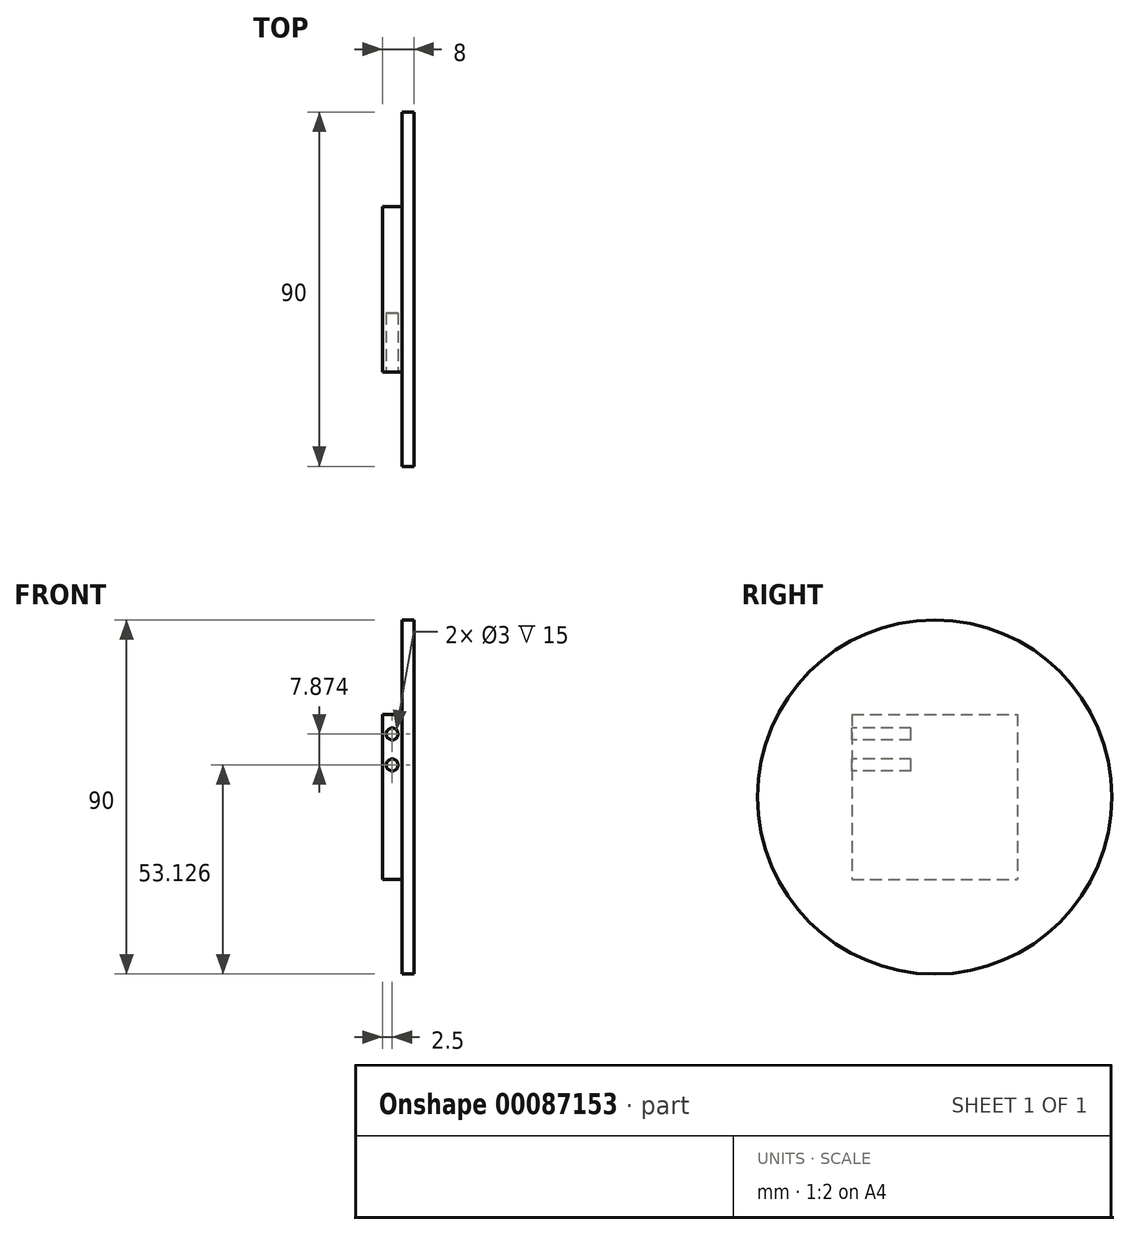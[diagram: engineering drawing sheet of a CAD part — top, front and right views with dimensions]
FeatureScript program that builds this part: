
annotation { "Feature Type Name" : "Feature", "Feature Type Description" : "" }
export const myFeature = defineFeature(function(context is Context, id is Id, definition is map)
    precondition{}
    {
        {
            var Q0;
            Q0=qCreatedBy(makeId("Right.planeOp"),FACE);
            var sketch = newSketch(context, id + "F0", { "sketchPlane" : qUnion([Q0])});
            skCircle(sketch, "E0", {"center": v(0, 0) * mm, "radius": 45 * mm, "construction": true});
            skLineSegment(sketch, "E1.bottom", {"start": v(-21, 21) * mm, "end": v(21, 21) * mm});
            skLineSegment(sketch, "E1.top", {"start": v(-21, -21) * mm, "end": v(21, -21) * mm});
            skLineSegment(sketch, "E1.left", {"start": v(-21, 21) * mm, "end": v(-21, -21) * mm});
            skLineSegment(sketch, "E1.right", {"start": v(21, 21) * mm, "end": v(21, -21) * mm});
            skSolve(sketch);
        }
        {
            var Q0;
            Q0 = qSketchRegion(id + "F0", true);
            extrude(context, id + "F1", {"entities" : qUnion([Q0]), "depth" : 5 * mm, "offsetDistance" : 25 * mm});
        }
        {
            var Q0;
            Q0=makeQuery(id+"F1.opExtrude","SWEPT_FACE",FACE,{"disambiguationData":[OSD([sQuery(id+"F0.wireOp",EDGE,"E1.left")])]});
            var sketch = newSketch(context, id + "F2", { "sketchPlane" : qUnion([Q0])});
            skCircle(sketch, "E2", {"center": v(2.5, 16) * mm, "radius": 1.5 * mm});
            skPoint(sketch, "E2.centerSnap0", {"position": v(2.5, 21) * mm});
            skCircle(sketch, "E3", {"center": v(2.5, 8.13) * mm, "radius": 1.5 * mm});
            skSolve(sketch);
        }
        {
            var Q0;
            Q0 = qSketchRegion(id + "F2", true);
            extrude(context, id + "F3", {"entities" : qUnion([Q0]), "operationType" : NewBodyOperationType.REMOVE, "oppositeDirection" : true, "depth" : 15 * mm, "offsetDistance" : 25 * mm});
        }
        {
            var Q0;
            Q0=qCreatedBy(makeId("Top.planeOp"),FACE);
            var sketch = newSketch(context, id + "F4", { "sketchPlane" : qUnion([Q0])});
            skLineSegment(sketch, "E4", {"start": v(0, 0) * mm, "end": v(84.42, 0) * mm});
            skSolve(sketch);
        }
        {
            var Q0;
            Q0=makeQuery(id+"F1.opExtrude","CAP_FACE",FACE,{"disambiguationData":[OSD([sQuery(id+"F0.wireOp",EDGE,"E1.bottom"),sQuery(id+"F0.wireOp",EDGE,"E1.top"),sQuery(id+"F0.wireOp",EDGE,"E1.left"),sQuery(id+"F0.wireOp",EDGE,"E1.right")])],"isStart":false});
            var sketch = newSketch(context, id + "F5", { "sketchPlane" : qUnion([Q0])});
            skCircle(sketch, "E5", {"center": v(0, 0) * mm, "radius": 45 * mm});
            skSolve(sketch);
        }
        {
            var Q0;
            Q0 = qSketchRegion(id + "F5", true);
            extrude(context, id + "F6", {"entities" : qUnion([Q0]), "operationType" : NewBodyOperationType.ADD, "depth" : 3 * mm, "offsetDistance" : 25 * mm});
        }
    });
